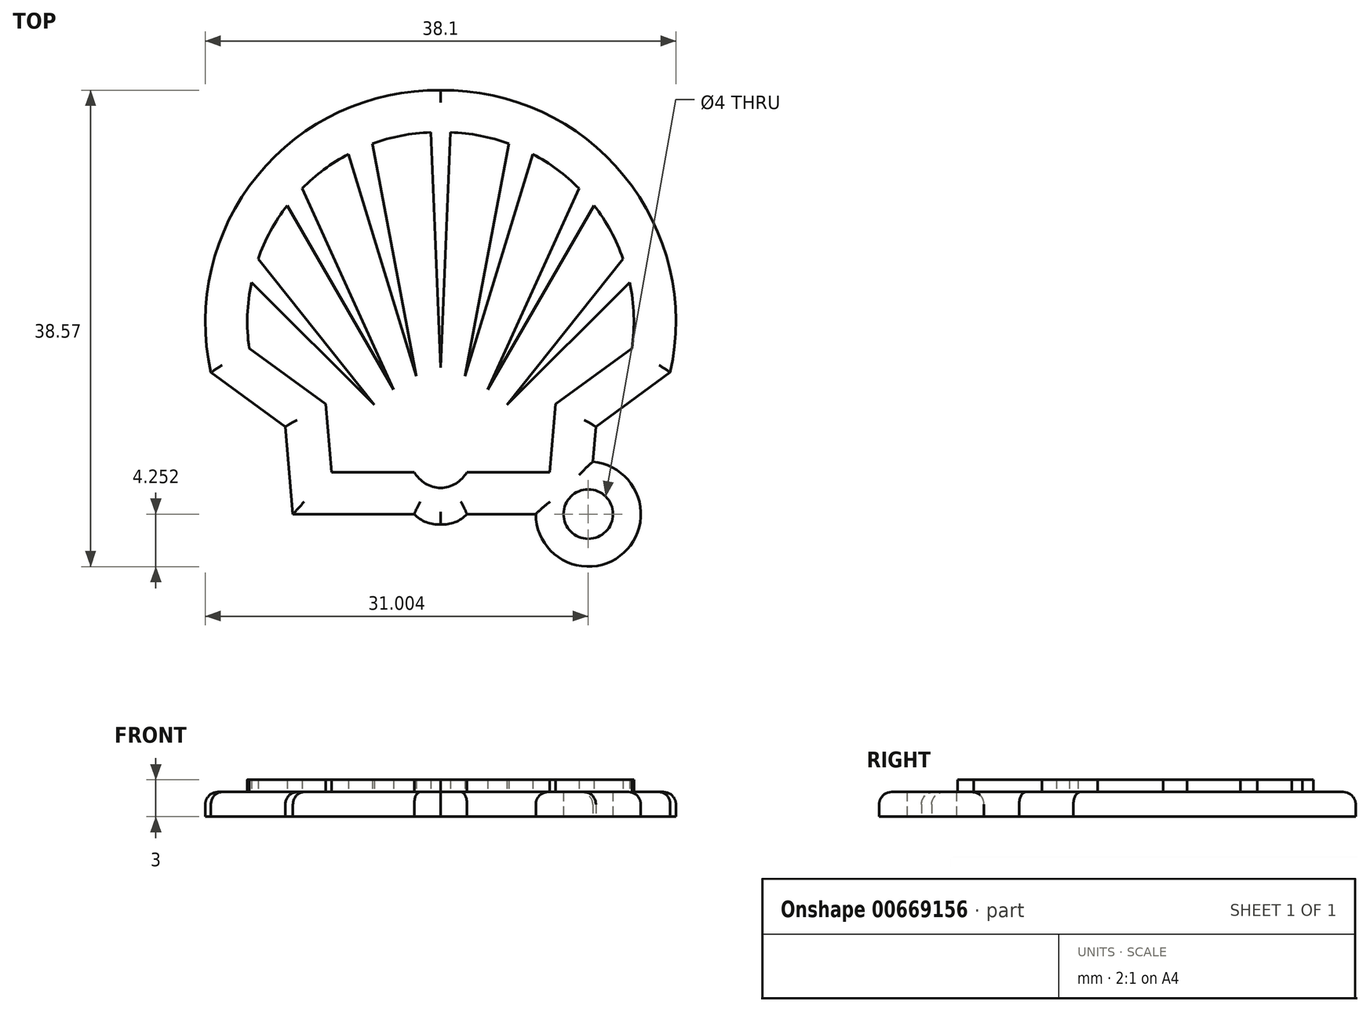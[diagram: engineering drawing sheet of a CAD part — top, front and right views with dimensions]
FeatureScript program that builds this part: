
annotation { "Feature Type Name" : "Feature", "Feature Type Description" : "" }
export const myFeature = defineFeature(function(context is Context, id is Id, definition is map)
    precondition{}
    {
        {
            var Q0;
            Q0=qCreatedBy(makeId("Top.planeOp"),FACE);
            var sketch = newSketch(context, id + "F0", { "sketchPlane" : qUnion([Q0])});
            skLineSegment(sketch, "E0", {"start": v(8.05, 1.8) * mm, "end": v(17.86, 1.8) * mm});
            skLineSegment(sketch, "E1", {"start": v(20, 0) * mm, "end": v(20, 37.06) * mm, "construction": true});
            skLineSegment(sketch, "E2", {"start": v(8.05, 1.8) * mm, "end": v(7.43, 8.87) * mm});
            skLineSegment(sketch, "E3", {"start": v(7.43, 8.87) * mm, "end": v(1.4, 13.26) * mm});
            skArc(sketch, "E4", {"start": v(20, 36.1) * mm, "mid": v(5.16, 29.2) * mm, "end": v(1.4, 13.26) * mm});
            skArc(sketch, "E5", {"start": v(17.86, 1.8) * mm, "mid": v(18.84, 1.13) * mm, "end": v(20, 0.97) * mm});
            skLineSegment(sketch, "E6.0", {"start": v(11.16, 5.2) * mm, "end": v(17.86, 5.2) * mm});
            skLineSegment(sketch, "E6.1", {"start": v(11.16, 5.2) * mm, "end": v(10.69, 10.7) * mm});
            skLineSegment(sketch, "E6.2", {"start": v(10.69, 10.7) * mm, "end": v(4.5, 15.21) * mm});
            skArc(sketch, "E7", {"start": v(17.86, 5.2) * mm, "mid": v(18.77, 4.27) * mm, "end": v(20, 3.9) * mm});
            skLineSegment(sketch, "E8", {"start": v(4.69, 20.54) * mm, "end": v(4.69, 20.54) * mm});
            skLineSegment(sketch, "E9", {"start": v(14.63, 10.65) * mm, "end": v(5.22, 22.45) * mm});
            skLineSegment(sketch, "E10", {"start": v(7.59, 26.78) * mm, "end": v(7.59, 26.78) * mm});
            skLineSegment(sketch, "E11", {"start": v(16.2, 11.88) * mm, "end": v(8.79, 28.15) * mm});
            skLineSegment(sketch, "E12", {"start": v(18.03, 12.95) * mm, "end": v(12.53, 30.93) * mm});
            skLineSegment(sketch, "E13", {"start": v(18.03, 12.95) * mm, "end": v(14.47, 31.79) * mm});
            skLineSegment(sketch, "E14", {"start": v(19.2, 32.7) * mm, "end": v(20, 13.64) * mm});
            skArc(sketch, "E15", {"start": v(12.53, 30.93) * mm, "mid": v(10.56, 29.68) * mm, "end": v(8.79, 28.15) * mm});
            skArc(sketch, "E16", {"start": v(19.2, 32.7) * mm, "mid": v(16.8, 32.43) * mm, "end": v(14.47, 31.79) * mm});
            skLineSegment(sketch, "E17", {"start": v(7.59, 26.78) * mm, "end": v(16.2, 11.88) * mm});
            skLineSegment(sketch, "E18", {"start": v(4.69, 20.54) * mm, "end": v(14.63, 10.65) * mm});
            skArc(sketch, "E19", {"start": v(4.69, 20.54) * mm, "mid": v(4.36, 17.88) * mm, "end": v(4.5, 15.21) * mm});
            skArc(sketch, "E20", {"start": v(7.59, 26.78) * mm, "mid": v(6.23, 24.71) * mm, "end": v(5.22, 22.45) * mm});
            skArc(sketch, "E21.MirrorCS", {"start": v(20, 36.1) * mm, "mid": v(34.84, 29.2) * mm, "end": v(38.6, 13.26) * mm});
            skArc(sketch, "E22.MirrorCS", {"start": v(20.8, 32.7) * mm, "mid": v(23.2, 32.43) * mm, "end": v(25.53, 31.79) * mm});
            skArc(sketch, "E23.MirrorCS", {"start": v(27.47, 30.93) * mm, "mid": v(29.44, 29.68) * mm, "end": v(31.21, 28.15) * mm});
            skArc(sketch, "E24.MirrorCS", {"start": v(32.41, 26.78) * mm, "mid": v(33.77, 24.71) * mm, "end": v(34.78, 22.45) * mm});
            skArc(sketch, "E25.MirrorCS", {"start": v(35.31, 20.54) * mm, "mid": v(35.64, 17.88) * mm, "end": v(35.5, 15.21) * mm});
            skLineSegment(sketch, "E26.MirrorCS", {"start": v(20.8, 32.7) * mm, "end": v(20, 13.64) * mm});
            skLineSegment(sketch, "E27.MirrorCS", {"start": v(21.97, 12.95) * mm, "end": v(25.53, 31.79) * mm});
            skLineSegment(sketch, "E28.MirrorCS", {"start": v(21.97, 12.95) * mm, "end": v(27.47, 30.93) * mm});
            skLineSegment(sketch, "E29.MirrorCS", {"start": v(23.8, 11.88) * mm, "end": v(31.21, 28.15) * mm});
            skLineSegment(sketch, "E30.MirrorCS", {"start": v(32.41, 26.78) * mm, "end": v(23.8, 11.88) * mm});
            skLineSegment(sketch, "E31.MirrorCS", {"start": v(25.37, 10.65) * mm, "end": v(34.78, 22.45) * mm});
            skLineSegment(sketch, "E32.MirrorCS", {"start": v(35.31, 20.54) * mm, "end": v(25.37, 10.65) * mm});
            skLineSegment(sketch, "E33.MirrorCS", {"start": v(29.31, 10.7) * mm, "end": v(35.5, 15.21) * mm});
            skLineSegment(sketch, "E34.MirrorCS", {"start": v(32.57, 8.87) * mm, "end": v(38.6, 13.26) * mm});
            skLineSegment(sketch, "E35.MirrorCS", {"start": v(28.84, 5.2) * mm, "end": v(29.31, 10.7) * mm});
            skLineSegment(sketch, "E36.MirrorCS", {"start": v(28.84, 5.2) * mm, "end": v(22.14, 5.2) * mm});
            skArc(sketch, "E37.MirrorCS", {"start": v(22.14, 1.8) * mm, "mid": v(21.16, 1.13) * mm, "end": v(20, 0.97) * mm});
            skArc(sketch, "E38.MirrorCS", {"start": v(22.14, 5.2) * mm, "mid": v(21.23, 4.27) * mm, "end": v(20, 3.9) * mm});
            skLineSegment(sketch, "E39", {"start": v(27.7, 1.8) * mm, "end": v(22.14, 1.8) * mm});
            skArc(sketch, "E40", {"start": v(27.7, 1.8) * mm, "mid": v(34.83, -1.34) * mm, "end": v(32.32, 6.03) * mm});
            skLineSegment(sketch, "E41", {"start": v(29.95, 1.8) * mm, "end": v(27.7, 1.8) * mm});
            skArc(sketch, "E42", {"start": v(29.95, 1.8) * mm, "mid": v(33.3, 0.32) * mm, "end": v(32.13, 3.78) * mm});
            skCircle(sketch, "E43", {"center": v(31.95, 1.8) * mm, "radius": 2 * mm});
            skLineSegment(sketch, "E44", {"start": v(32.13, 3.78) * mm, "end": v(32.57, 8.87) * mm});
            skSolve(sketch);
        }
        {
            var Q0;
            Q0=makeQuery(id+"F0.imprint","IMPRINT",FACE,{"disambiguationData":[TD([[makeQuery(id+"F0.imprint","IMPRINT",EDGE,{"derivedFrom":sQuery(id+"F0.wireOp",EDGE,"E0")}),1.0]])]});
            var Q1;
            {var subQ0=sQuery(id+"F0.wireOp",EDGE,"E40");Q1=makeQuery(id+"F0.imprint","IMPRINT",FACE,{"disambiguationData":[TD([[makeQuery(id+"F0.imprint","IMPRINT",EDGE,{"derivedFrom":subQ0}),1.0]])]});}
            extrude(context, id + "F1", {"entities" : qUnion([Q0, Q1]), "depth" : 2 * mm, "offsetDistance" : 25 * mm});
        }
        {
            var Q0;
            Q0=makeQuery(id+"F0.imprint","IMPRINT",FACE,{"disambiguationData":[TD([[makeQuery(id+"F0.imprint","IMPRINT",EDGE,{"derivedFrom":sQuery(id+"F0.wireOp",EDGE,"E6.0")}),1.0]])]});
            extrude(context, id + "F2", {"entities" : qUnion([Q0]), "operationType" : NewBodyOperationType.ADD, "depth" : 3 * mm, "offsetDistance" : 25 * mm});
        }
        {
            var Q0;
            Q0=makeQuery(id+"F1.opExtrude","CAP_EDGE",EDGE,{"disambiguationData":[OSD([sQuery(id+"F0.wireOp",EDGE,"E0")])],"isStart":false});
            var Q1;
            Q1=makeQuery(id+"F1.opExtrude","CAP_EDGE",EDGE,{"disambiguationData":[OSD([sQuery(id+"F0.wireOp",EDGE,"E5")])],"isStart":false});
            var Q2;
            Q2=makeQuery(id+"F1.opExtrude","CAP_EDGE",EDGE,{"disambiguationData":[OSD([sQuery(id+"F0.wireOp",EDGE,"E37.MirrorCS")])],"isStart":false});
            var Q3;
            Q3=makeQuery(id+"F1.opExtrude","CAP_EDGE",EDGE,{"disambiguationData":[OSD([sQuery(id+"F0.wireOp",EDGE,"E39")])],"isStart":false});
            var Q4;
            Q4=makeQuery(id+"F1.opExtrude","CAP_EDGE",EDGE,{"disambiguationData":[OSD([sQuery(id+"F0.wireOp",EDGE,"E40")])],"isStart":false});
            var Q5;
            Q5=makeQuery(id+"F1.opExtrude","CAP_EDGE",EDGE,{"disambiguationData":[OSD([sQuery(id+"F0.wireOp",EDGE,"E44")])],"isStart":false});
            var Q6;
            Q6=makeQuery(id+"F1.opExtrude","CAP_EDGE",EDGE,{"disambiguationData":[OSD([sQuery(id+"F0.wireOp",EDGE,"E34.MirrorCS")])],"isStart":false});
            var Q7;
            Q7=makeQuery(id+"F1.opExtrude","CAP_EDGE",EDGE,{"disambiguationData":[OSD([sQuery(id+"F0.wireOp",EDGE,"E3")])],"isStart":false});
            var Q8;
            Q8=makeQuery(id+"F1.opExtrude","CAP_EDGE",EDGE,{"disambiguationData":[OSD([sQuery(id+"F0.wireOp",EDGE,"E2")])],"isStart":false});
            var Q9;
            Q9=makeQuery(id+"F1.opExtrude","CAP_EDGE",EDGE,{"disambiguationData":[OSD([sQuery(id+"F0.wireOp",EDGE,"E4")])],"isStart":false});
            var Q10;
            Q10=makeQuery(id+"F1.opExtrude","CAP_EDGE",EDGE,{"disambiguationData":[OSD([sQuery(id+"F0.wireOp",EDGE,"E21.MirrorCS")])],"isStart":false});
            fillet(context, id + "F3", {"entities" : qUnion([Q0, Q1, Q2, Q3, Q4, Q5, Q6, Q7, Q8, Q9, Q10]), "radius" : 1 * mm, "tangentPropagation" : true, "allowEdgeOverflow" : false});
        }
    });
